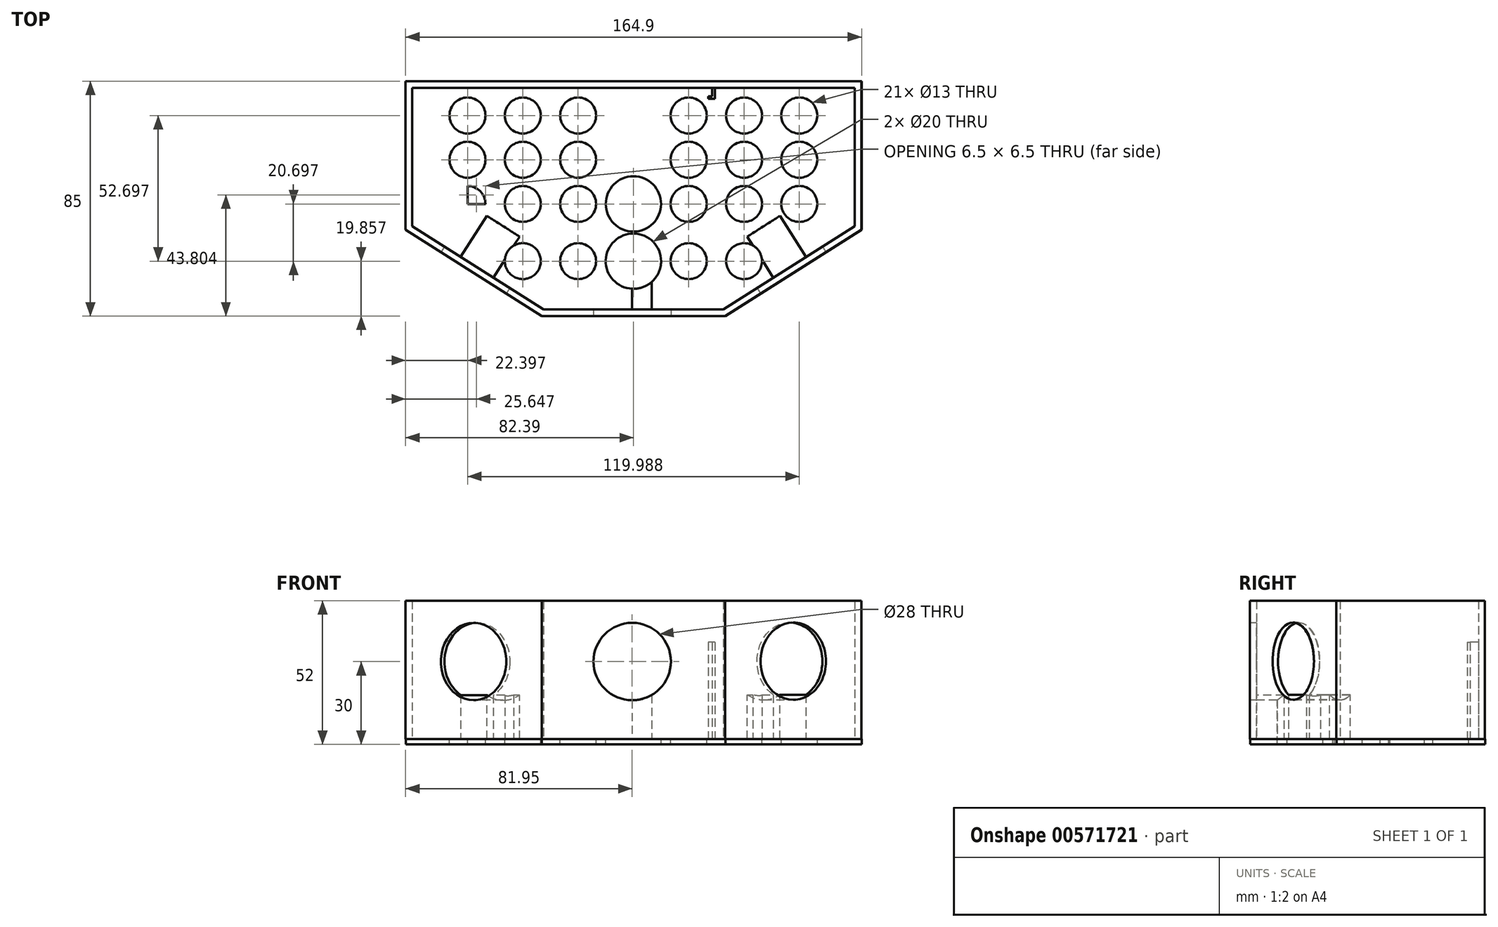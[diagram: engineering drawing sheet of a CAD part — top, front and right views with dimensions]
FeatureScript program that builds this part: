
annotation { "Feature Type Name" : "Feature", "Feature Type Description" : "" }
export const myFeature = defineFeature(function(context is Context, id is Id, definition is map)
    precondition{}
    {
        {
            var Q0;
            Q0=qCreatedBy(makeId("Top.planeOp"),FACE);
            var sketch = newSketch(context, id + "F0", { "sketchPlane" : qUnion([Q0])});
            skLineSegment(sketch, "E0.bottom", {"start": v(80.43, 34.87) * mm, "end": v(29.94, 34.87) * mm});
            skLineSegment(sketch, "E0.top", {"start": v(32.94, -45.28) * mm, "end": v(-32.06, -45.28) * mm});
            skLineSegment(sketch, "E0.left", {"start": v(80.43, 34.87) * mm, "end": v(80.43, -15.13) * mm});
            skLineSegment(sketch, "E0.right", {"start": v(-79.55, 34.87) * mm, "end": v(-79.55, -15.13) * mm});
            skPoint(sketch, "E0.middle", {"position": v(0, 0) * mm});
            skPoint(sketch, "E1", {"position": v(-79.55, -15.13) * mm});
            skPoint(sketch, "E2", {"position": v(80.43, -15.13) * mm});
            skPoint(sketch, "E3", {"position": v(32.94, -45.28) * mm});
            skPoint(sketch, "E4", {"position": v(-32.06, -45.28) * mm});
            skLineSegment(sketch, "E5", {"start": v(-79.55, -15.13) * mm, "end": v(-32.06, -45.28) * mm});
            skLineSegment(sketch, "E6", {"start": v(32.94, -45.28) * mm, "end": v(80.43, -15.13) * mm});
            skLineSegment(sketch, "E7", {"start": v(-55.8, -30.2) * mm, "end": v(-44.16, -37.6) * mm});
            skLineSegment(sketch, "E8", {"start": v(0.44, -45.28) * mm, "end": v(14.24, -45.28) * mm});
            skLineSegment(sketch, "E9", {"start": v(56.69, -30.2) * mm, "end": v(45.04, -37.6) * mm});
            skLineSegment(sketch, "E10", {"start": v(0.44, 34.87) * mm, "end": v(28.94, 34.87) * mm});
            skLineSegment(sketch, "E11", {"start": v(28.94, 34.87) * mm, "end": v(28.94, 31.87) * mm});
            skLineSegment(sketch, "E12", {"start": v(28.94, 31.87) * mm, "end": v(27.44, 31.87) * mm});
            skLineSegment(sketch, "E13", {"start": v(0.44, 34.87) * mm, "end": v(-28.06, 34.87) * mm});
            skLineSegment(sketch, "E14", {"start": v(-28.06, 31.87) * mm, "end": v(-26.56, 31.87) * mm});
            skLineSegment(sketch, "E15", {"start": v(-26.56, 31.87) * mm, "end": v(-28.06, 31.87) * mm});
            skLineSegment(sketch, "E16", {"start": v(-28.06, 34.87) * mm, "end": v(-28.06, 31.87) * mm});
            skLineSegment(sketch, "E17.0", {"start": v(82.83, 37.27) * mm, "end": v(-81.95, 37.27) * mm});
            skLineSegment(sketch, "E17.1", {"start": v(33.64, -47.68) * mm, "end": v(82.83, -16.45) * mm});
            skLineSegment(sketch, "E17.2", {"start": v(33.64, -47.68) * mm, "end": v(-32.76, -47.68) * mm});
            skLineSegment(sketch, "E17.3", {"start": v(82.83, 37.27) * mm, "end": v(82.83, -16.45) * mm});
            skLineSegment(sketch, "E17.4", {"start": v(-81.95, -16.45) * mm, "end": v(-32.76, -47.68) * mm});
            skLineSegment(sketch, "E17.5", {"start": v(-81.95, 37.27) * mm, "end": v(-81.95, -16.45) * mm});
            skLineSegment(sketch, "E18.0", {"start": v(-26.56, 30.87) * mm, "end": v(-29.06, 30.87) * mm});
            skLineSegment(sketch, "E18.1", {"start": v(-29.06, 34.87) * mm, "end": v(-29.06, 30.87) * mm});
            skLineSegment(sketch, "E19.0", {"start": v(29.94, 30.87) * mm, "end": v(27.44, 30.87) * mm});
            skLineSegment(sketch, "E19.1", {"start": v(29.94, 34.87) * mm, "end": v(29.94, 30.87) * mm});
            skLineSegment(sketch, "E20", {"start": v(-26.56, 30.87) * mm, "end": v(-26.56, 31.87) * mm});
            skLineSegment(sketch, "E21", {"start": v(27.44, 30.87) * mm, "end": v(27.44, 31.87) * mm});
            skLineSegment(sketch, "E22.trimOffspring", {"start": v(-29.06, 34.87) * mm, "end": v(-79.55, 34.87) * mm});
            skLineSegment(sketch, "E23.trimOffspring", {"start": v(28.94, 34.87) * mm, "end": v(-28.06, 34.87) * mm});
            skLineSegment(sketch, "E24", {"start": v(-79.55, 34.87) * mm, "end": v(-59.55, 34.87) * mm});
            skLineSegment(sketch, "E25", {"start": v(80.43, 34.87) * mm, "end": v(60.43, 34.87) * mm});
            skLineSegment(sketch, "E26", {"start": v(-59.55, 34.87) * mm, "end": v(-59.55, -27.82) * mm});
            skLineSegment(sketch, "E27", {"start": v(-59.55, -27.82) * mm, "end": v(60.43, -27.82) * mm});
            skLineSegment(sketch, "E28", {"start": v(60.43, -27.82) * mm, "end": v(60.43, 34.87) * mm});
            skLineSegment(sketch, "E29", {"start": v(60.43, 34.87) * mm, "end": v(60.43, 24.87) * mm});
            skLineSegment(sketch, "E30", {"start": v(60.43, 24.87) * mm, "end": v(-59.55, 24.87) * mm});
            skLineSegment(sketch, "E31", {"start": v(-59.55, 34.87) * mm, "end": v(-39.55, 34.87) * mm});
            skLineSegment(sketch, "E32", {"start": v(-39.55, 34.87) * mm, "end": v(-19.55, 34.87) * mm});
            skLineSegment(sketch, "E33", {"start": v(60.43, 34.87) * mm, "end": v(40.43, 34.87) * mm});
            skLineSegment(sketch, "E34", {"start": v(40.43, 34.87) * mm, "end": v(20.43, 34.87) * mm});
            skLineSegment(sketch, "E35", {"start": v(60.43, -27.82) * mm, "end": v(40.43, -27.82) * mm});
            skLineSegment(sketch, "E36", {"start": v(40.43, -27.82) * mm, "end": v(20.43, -27.82) * mm});
            skLineSegment(sketch, "E37", {"start": v(-59.55, -27.82) * mm, "end": v(-39.55, -27.82) * mm});
            skLineSegment(sketch, "E38", {"start": v(-39.55, -27.82) * mm, "end": v(-19.55, -27.82) * mm});
            skLineSegment(sketch, "E39", {"start": v(-39.55, 34.87) * mm, "end": v(-39.55, -27.82) * mm});
            skLineSegment(sketch, "E40", {"start": v(-19.55, -27.82) * mm, "end": v(-19.55, 34.87) * mm});
            skLineSegment(sketch, "E41", {"start": v(20.43, 34.87) * mm, "end": v(20.43, -27.82) * mm});
            skLineSegment(sketch, "E42", {"start": v(40.43, -27.82) * mm, "end": v(40.43, 34.87) * mm});
            skCircle(sketch, "E43", {"center": v(-59.55, 24.87) * mm, "radius": 6.5 * mm});
            skCircle(sketch, "E44", {"center": v(-19.55, -27.82) * mm, "radius": 6.5 * mm});
            skCircle(sketch, "E45", {"center": v(20.43, -27.82) * mm, "radius": 6.5 * mm});
            skLineSegment(sketch, "E46", {"start": v(-59.55, 24.87) * mm, "end": v(-39.55, 24.87) * mm});
            skLineSegment(sketch, "E47", {"start": v(-39.55, 24.87) * mm, "end": v(-19.55, 24.87) * mm});
            skLineSegment(sketch, "E48", {"start": v(-19.55, 24.87) * mm, "end": v(20.43, 24.87) * mm});
            skLineSegment(sketch, "E49", {"start": v(20.43, 24.87) * mm, "end": v(40.43, 24.87) * mm});
            skLineSegment(sketch, "E50", {"start": v(40.43, 24.87) * mm, "end": v(60.43, 24.87) * mm});
            skCircle(sketch, "E51", {"center": v(-39.55, 24.87) * mm, "radius": 6.5 * mm});
            skCircle(sketch, "E52", {"center": v(-19.55, 24.87) * mm, "radius": 6.5 * mm});
            skCircle(sketch, "E53", {"center": v(20.43, 24.87) * mm, "radius": 6.5 * mm});
            skCircle(sketch, "E54", {"center": v(40.43, 24.87) * mm, "radius": 6.5 * mm});
            skCircle(sketch, "E55", {"center": v(60.43, 24.87) * mm, "radius": 6.5 * mm});
            skLineSegment(sketch, "E56", {"start": v(-59.55, 24.87) * mm, "end": v(-59.55, 8.87) * mm});
            skLineSegment(sketch, "E57", {"start": v(-59.55, 8.87) * mm, "end": v(-59.55, -7.13) * mm});
            skLineSegment(sketch, "E58", {"start": v(-59.55, -7.13) * mm, "end": v(-59.55, -11.32) * mm});
            skLineSegment(sketch, "E59", {"start": v(60.43, 24.87) * mm, "end": v(60.43, 8.87) * mm});
            skLineSegment(sketch, "E60", {"start": v(60.43, 8.87) * mm, "end": v(60.43, -7.13) * mm});
            skLineSegment(sketch, "E61", {"start": v(-59.55, 8.87) * mm, "end": v(60.43, 8.87) * mm});
            skLineSegment(sketch, "E62", {"start": v(60.43, -7.13) * mm, "end": v(-59.55, -7.13) * mm});
            skLineSegment(sketch, "E63", {"start": v(-39.55, 8.87) * mm, "end": v(-19.55, 8.87) * mm});
            skLineSegment(sketch, "E64", {"start": v(-19.55, 8.87) * mm, "end": v(-19.55, -7.13) * mm});
            skLineSegment(sketch, "E65", {"start": v(-19.55, -7.13) * mm, "end": v(-39.55, -7.13) * mm});
            skLineSegment(sketch, "E66", {"start": v(-39.55, -7.13) * mm, "end": v(-19.55, -7.13) * mm});
            skLineSegment(sketch, "E67", {"start": v(20.43, 8.87) * mm, "end": v(40.43, 8.87) * mm});
            skLineSegment(sketch, "E68", {"start": v(40.43, 8.87) * mm, "end": v(60.43, 8.87) * mm});
            skLineSegment(sketch, "E69", {"start": v(60.43, -7.13) * mm, "end": v(40.43, -7.13) * mm});
            skLineSegment(sketch, "E70", {"start": v(40.43, -7.13) * mm, "end": v(20.43, -7.13) * mm});
            skCircle(sketch, "E71", {"center": v(-59.55, 8.87) * mm, "radius": 6.5 * mm});
            skCircle(sketch, "E72", {"center": v(-59.55, -7.13) * mm, "radius": 6.5 * mm});
            skCircle(sketch, "E73", {"center": v(-39.55, -7.13) * mm, "radius": 6.5 * mm});
            skCircle(sketch, "E74", {"center": v(-39.55, 8.87) * mm, "radius": 6.5 * mm});
            skCircle(sketch, "E75", {"center": v(-19.55, 8.87) * mm, "radius": 6.5 * mm});
            skCircle(sketch, "E76", {"center": v(-19.55, -7.13) * mm, "radius": 6.5 * mm});
            skCircle(sketch, "E77", {"center": v(20.43, 8.87) * mm, "radius": 6.5 * mm});
            skCircle(sketch, "E78", {"center": v(40.43, 8.87) * mm, "radius": 6.5 * mm});
            skCircle(sketch, "E79", {"center": v(60.43, 8.87) * mm, "radius": 6.5 * mm});
            skCircle(sketch, "E80", {"center": v(60.43, -7.13) * mm, "radius": 6.5 * mm});
            skCircle(sketch, "E81", {"center": v(40.43, -7.13) * mm, "radius": 6.5 * mm});
            skCircle(sketch, "E82", {"center": v(20.43, -7.13) * mm, "radius": 6.5 * mm});
            skLineSegment(sketch, "E83", {"start": v(-19.55, -27.82) * mm, "end": v(0.44, -27.82) * mm});
            skLineSegment(sketch, "E84", {"start": v(0.44, -27.82) * mm, "end": v(0.44, 34.87) * mm});
            skLineSegment(sketch, "E85", {"start": v(0.44, 24.87) * mm, "end": v(0.44, 8.87) * mm});
            skLineSegment(sketch, "E86", {"start": v(0.44, 8.87) * mm, "end": v(0.44, -7.13) * mm});
            skLineSegment(sketch, "E87", {"start": v(0.44, -7.13) * mm, "end": v(0.44, -27.82) * mm});
            skCircle(sketch, "E88", {"center": v(0.44, -27.82) * mm, "radius": 10 * mm});
            skCircle(sketch, "E89", {"center": v(0.44, -7.13) * mm, "radius": 10 * mm});
            skCircle(sketch, "E90", {"center": v(0.44, 24.87) * mm, "radius": 9.5 * mm});
            skCircle(sketch, "E91", {"center": v(-39.55, -27.82) * mm, "radius": 6.5 * mm});
            skCircle(sketch, "E92", {"center": v(40.43, -27.82) * mm, "radius": 6.5 * mm});
            skSolve(sketch);
        }
        {
            var Q0;
            Q0 = qSketchRegion(id + "F0", true);
            extrude(context, id + "F1", {"entities" : qUnion([Q0]), "depth" : 50 * mm, "offsetDistance" : 25 * mm});
        }
        {
            var Q0;
            Q0=qCreatedBy(makeId("Top.planeOp"),FACE);
            var sketch = newSketch(context, id + "F2", { "sketchPlane" : qUnion([Q0])});
            skLineSegment(sketch, "E93.0", {"start": v(82.95, 37.32) * mm, "end": v(-81.84, 37.32) * mm});
            skLineSegment(sketch, "E93.1", {"start": v(33.75, -47.63) * mm, "end": v(82.95, -16.4) * mm});
            skLineSegment(sketch, "E93.2", {"start": v(33.75, -47.63) * mm, "end": v(-32.64, -47.63) * mm});
            skLineSegment(sketch, "E93.3", {"start": v(82.95, 37.32) * mm, "end": v(82.95, -16.4) * mm});
            skLineSegment(sketch, "E93.4", {"start": v(-81.84, -16.4) * mm, "end": v(-32.64, -47.63) * mm});
            skLineSegment(sketch, "E93.5", {"start": v(-81.84, 37.32) * mm, "end": v(-81.84, -16.4) * mm});
            skSolve(sketch);
        }
        {
            var Q0;
            Q0=makeQuery(id+"F1.opExtrude","SWEPT_FACE",FACE,{"disambiguationData":[OSD([sQuery(id+"F0.wireOp",EDGE,"E17.1")])]});
            var sketch = newSketch(context, id + "F3", { "sketchPlane" : qUnion([Q0])});
            skCircle(sketch, "E94", {"center": v(31.98, 28.12) * mm, "radius": 14 * mm});
            skLineSegment(sketch, "E95", {"start": v(31.98, 14.12) * mm, "end": v(31.98, 0) * mm});
            skPoint(sketch, "E95.startSnap0", {"position": v(31.98, 0) * mm});
            skLineSegment(sketch, "E96", {"start": v(31.98, 0) * mm, "end": v(38.98, 0) * mm});
            skLineSegment(sketch, "E97", {"start": v(31.98, 0) * mm, "end": v(24.98, 0) * mm});
            skLineSegment(sketch, "E98", {"start": v(24.98, 0) * mm, "end": v(24.98, 16) * mm});
            skLineSegment(sketch, "E99", {"start": v(38.98, 0) * mm, "end": v(38.98, 16) * mm});
            skSolve(sketch);
        }
        {
            var Q0;
            Q0=makeQuery(id+"F3.imprint","IMPRINT",FACE,{"disambiguationData":[TD([[makeQuery(id+"F3.imprint","IMPRINT",EDGE,{"derivedFrom":sQuery(id+"F3.wireOp",EDGE,"E94")}),1.0]])]});
            extrude(context, id + "F4", {"entities" : qUnion([Q0]), "operationType" : NewBodyOperationType.REMOVE, "oppositeDirection" : true, "depth" : 28 * mm, "offsetDistance" : 25 * mm});
        }
        {
            var Q0;
            Q0=makeQuery(id+"F1.opExtrude","SWEPT_FACE",FACE,{"disambiguationData":[OSD([sQuery(id+"F0.wireOp",EDGE,"E17.2")])]});
            var sketch = newSketch(context, id + "F5", { "sketchPlane" : qUnion([Q0])});
            skLineSegment(sketch, "E100", {"start": v(0, 0) * mm, "end": v(0, 28) * mm});
            skLineSegment(sketch, "E101", {"start": v(0, 28) * mm, "end": v(14, 28) * mm});
            skCircle(sketch, "E102", {"center": v(0, 28) * mm, "radius": 14 * mm});
            skLineSegment(sketch, "E103", {"start": v(0, 0) * mm, "end": v(-7, 0) * mm});
            skLineSegment(sketch, "E104", {"start": v(-7, 0) * mm, "end": v(0, 0) * mm});
            skLineSegment(sketch, "E105", {"start": v(-7, 0) * mm, "end": v(-7, 15.88) * mm});
            skLineSegment(sketch, "E106", {"start": v(-7, 15.88) * mm, "end": v(-7, 0) * mm});
            skLineSegment(sketch, "E107", {"start": v(0, 0) * mm, "end": v(7, 0) * mm});
            skLineSegment(sketch, "E108", {"start": v(7, 0) * mm, "end": v(7, 15.88) * mm});
            skLineSegment(sketch, "E109", {"start": v(7, 15.88) * mm, "end": v(7, 0) * mm});
            skSolve(sketch);
        }
        {
            var Q0;
            Q0 = qSketchRegion(id + "F2", true);
            extrude(context, id + "F6", {"entities" : qUnion([Q0]), "operationType" : NewBodyOperationType.ADD, "oppositeDirection" : true, "depth" : 2 * mm, "offsetDistance" : 25 * mm});
        }
        {
            var Q0;
            {var subQ0=sQuery(id+"F5.wireOp",EDGE,"E101");Q0=makeQuery(id+"F5.imprint","IMPRINT",FACE,{"disambiguationData":[TD([[makeQuery(id+"F5.imprint","IMPRINT",EDGE,{"derivedFrom":subQ0}),-1.0]])]});}
            var Q1;
            {var subQ0=sQuery(id+"F5.wireOp",EDGE,"E101");Q1=makeQuery(id+"F5.imprint","IMPRINT",FACE,{"disambiguationData":[TD([[makeQuery(id+"F5.imprint","IMPRINT",EDGE,{"derivedFrom":subQ0}),1.0]])]});}
            extrude(context, id + "F7", {"entities" : qUnion([Q0, Q1]), "operationType" : NewBodyOperationType.REMOVE, "oppositeDirection" : true, "depth" : 20.7 * mm, "offsetDistance" : 25 * mm});
        }
        {
            var Q0;
            Q0=makeQuery(id+"F1.opExtrude","SWEPT_FACE",FACE,{"disambiguationData":[OSD([sQuery(id+"F0.wireOp",EDGE,"E17.4")])]});
            var sketch = newSketch(context, id + "F8", { "sketchPlane" : qUnion([Q0])});
            skLineSegment(sketch, "E110", {"start": v(-31.24, 0) * mm, "end": v(-31.24, 28) * mm});
            skLineSegment(sketch, "E111", {"start": v(-31.24, 28) * mm, "end": v(-45.24, 28) * mm});
            skCircle(sketch, "E112", {"center": v(-31.24, 28) * mm, "radius": 14 * mm});
            skLineSegment(sketch, "E113", {"start": v(-31.24, 0) * mm, "end": v(-38.24, 0) * mm});
            skLineSegment(sketch, "E114", {"start": v(-38.24, 0) * mm, "end": v(-38.24, 15.88) * mm});
            skLineSegment(sketch, "E115", {"start": v(-24.24, 0) * mm, "end": v(-24.24, 15.88) * mm});
            skSolve(sketch);
        }
        {
            var Q0;
            {var subQ0=sQuery(id+"F8.wireOp",EDGE,"E111");Q0=makeQuery(id+"F8.imprint","IMPRINT",FACE,{"disambiguationData":[TD([[makeQuery(id+"F8.imprint","IMPRINT",EDGE,{"derivedFrom":subQ0}),-1.0]])]});}
            var Q1;
            {var subQ0=sQuery(id+"F8.wireOp",EDGE,"E111");Q1=makeQuery(id+"F8.imprint","IMPRINT",FACE,{"disambiguationData":[TD([[makeQuery(id+"F8.imprint","IMPRINT",EDGE,{"derivedFrom":subQ0}),1.0]])]});}
            extrude(context, id + "F9", {"entities" : qUnion([Q0, Q1]), "operationType" : NewBodyOperationType.REMOVE, "oppositeDirection" : true, "depth" : 25 * mm, "offsetDistance" : 25 * mm});
        }
        {
            var Q0;
            {var subQ0=sQuery(id+"F5.wireOp",EDGE,"E104");Q0=makeQuery(id+"F5.imprint","IMPRINT",FACE,{"disambiguationData":[TD([[makeQuery(id+"F5.imprint","IMPRINT",EDGE,{"derivedFrom":subQ0}),-1.0]])]});}
            var Q1;
            {var subQ0=sQuery(id+"F5.wireOp",EDGE,"E107");Q1=makeQuery(id+"F5.imprint","IMPRINT",FACE,{"disambiguationData":[TD([[makeQuery(id+"F5.imprint","IMPRINT",EDGE,{"derivedFrom":subQ0}),-1.0]])]});}
            extrude(context, id + "F10", {"entities" : qUnion([Q0, Q1]), "operationType" : NewBodyOperationType.ADD, "oppositeDirection" : true, "depth" : 20 * mm, "offsetDistance" : 25 * mm});
        }
        {
            var Q0;
            {var subQ0=sQuery(id+"F8.wireOp",EDGE,"E113");Q0=makeQuery(id+"F8.imprint","IMPRINT",FACE,{"disambiguationData":[TD([[makeQuery(id+"F8.imprint","IMPRINT",EDGE,{"derivedFrom":subQ0}),1.0]])]});}
            var Q1;
            {var subQ6=sQuery(id+"F8.wireOp",EDGE,"E115");Q1=makeQuery(id+"F8.imprint","IMPRINT",FACE,{"disambiguationData":[TD([[makeQuery(id+"F8.imprint","IMPRINT",EDGE,{"derivedFrom":subQ6}),1.0]])]});}
            extrude(context, id + "F11", {"entities" : qUnion([Q0, Q1]), "operationType" : NewBodyOperationType.ADD, "oppositeDirection" : true, "depth" : 20 * mm, "offsetDistance" : 25 * mm});
        }
        {
            var Q0;
            {var subQ0=sQuery(id+"F3.wireOp",EDGE,"E95");Q0=makeQuery(id+"F3.imprint","IMPRINT",FACE,{"disambiguationData":[TD([[makeQuery(id+"F3.imprint","IMPRINT",EDGE,{"derivedFrom":subQ0}),-1.0]])]});}
            var Q1;
            {var subQ0=sQuery(id+"F3.wireOp",EDGE,"E95");Q1=makeQuery(id+"F3.imprint","IMPRINT",FACE,{"disambiguationData":[TD([[makeQuery(id+"F3.imprint","IMPRINT",EDGE,{"derivedFrom":subQ0}),1.0]])]});}
            extrude(context, id + "F12", {"entities" : qUnion([Q0, Q1]), "operationType" : NewBodyOperationType.ADD, "oppositeDirection" : true, "depth" : 20 * mm, "offsetDistance" : 25 * mm});
        }
        {
            var Q0;
            {var subQ1=sQuery(id+"F0.wireOp",EDGE,"E26");var subQ3=sQuery(id+"F0.wireOp",EDGE,"E43");var subQ4=makeQuery(id+"F0.imprint","INTERSECT",VERTEX,{"derivedFrom":[subQ1,subQ3]});Q0=makeQuery(id+"F0.imprint","IMPRINT",FACE,{"disambiguationData":[TD([[makeQuery(id+"F0.imprint","IMPRINT",EDGE,{"disambiguationData":[TD([[subQ4,-1.0]])],"derivedFrom":subQ3}),1.0]])]});}
            var Q1;
            {var subQ1=sQuery(id+"F0.wireOp",EDGE,"E26");var subQ3=sQuery(id+"F0.wireOp",EDGE,"E43");var subQ4=makeQuery(id+"F0.imprint","INTERSECT",VERTEX,{"derivedFrom":[subQ1,subQ3]});Q1=makeQuery(id+"F0.imprint","IMPRINT",FACE,{"disambiguationData":[TD([[makeQuery(id+"F0.imprint","IMPRINT",EDGE,{"disambiguationData":[TD([[subQ4,1.0]])],"derivedFrom":subQ3}),1.0]])]});}
            var Q2;
            {var subQ0=sQuery(id+"F0.wireOp",EDGE,"E46");var subQ1=sQuery(id+"F0.wireOp",EDGE,"E43");var subQ2=makeQuery(id+"F0.imprint","INTERSECT",VERTEX,{"derivedFrom":[subQ1,subQ0]});Q2=makeQuery(id+"F0.imprint","IMPRINT",FACE,{"disambiguationData":[TD([[makeQuery(id+"F0.imprint","IMPRINT",EDGE,{"disambiguationData":[TD([[subQ2,1.0]])],"derivedFrom":subQ1}),1.0]])]});}
            var Q3;
            {var subQ1=sQuery(id+"F0.wireOp",EDGE,"E39");var subQ3=sQuery(id+"F0.wireOp",EDGE,"E51");var subQ4=makeQuery(id+"F0.imprint","INTERSECT",VERTEX,{"disambiguationData":[OD(0.0)],"derivedFrom":[subQ1,subQ3]});Q3=makeQuery(id+"F0.imprint","IMPRINT",FACE,{"disambiguationData":[TD([[makeQuery(id+"F0.imprint","IMPRINT",EDGE,{"disambiguationData":[TD([[subQ4,-1.0]])],"derivedFrom":subQ3}),1.0]])]});}
            var Q4;
            {var subQ1=sQuery(id+"F0.wireOp",EDGE,"E39");var subQ3=sQuery(id+"F0.wireOp",EDGE,"E51");var subQ4=makeQuery(id+"F0.imprint","INTERSECT",VERTEX,{"disambiguationData":[OD(0.0)],"derivedFrom":[subQ1,subQ3]});Q4=makeQuery(id+"F0.imprint","IMPRINT",FACE,{"disambiguationData":[TD([[makeQuery(id+"F0.imprint","IMPRINT",EDGE,{"disambiguationData":[TD([[subQ4,1.0]])],"derivedFrom":subQ3}),1.0]])]});}
            var Q5;
            {var subQ1=sQuery(id+"F0.wireOp",EDGE,"E39");var subQ3=sQuery(id+"F0.wireOp",EDGE,"E51");var subQ4=makeQuery(id+"F0.imprint","INTERSECT",VERTEX,{"disambiguationData":[OD(1.0)],"derivedFrom":[subQ1,subQ3]});Q5=makeQuery(id+"F0.imprint","IMPRINT",FACE,{"disambiguationData":[TD([[makeQuery(id+"F0.imprint","IMPRINT",EDGE,{"disambiguationData":[TD([[subQ4,-1.0]])],"derivedFrom":subQ3}),1.0]])]});}
            var Q6;
            {var subQ1=sQuery(id+"F0.wireOp",EDGE,"E39");var subQ3=sQuery(id+"F0.wireOp",EDGE,"E51");var subQ4=makeQuery(id+"F0.imprint","INTERSECT",VERTEX,{"disambiguationData":[OD(1.0)],"derivedFrom":[subQ1,subQ3]});Q6=makeQuery(id+"F0.imprint","IMPRINT",FACE,{"disambiguationData":[TD([[makeQuery(id+"F0.imprint","IMPRINT",EDGE,{"disambiguationData":[TD([[subQ4,1.0]])],"derivedFrom":subQ3}),1.0]])]});}
            var Q7;
            {var subQ1=sQuery(id+"F0.wireOp",EDGE,"E40");var subQ3=sQuery(id+"F0.wireOp",EDGE,"E52");var subQ4=makeQuery(id+"F0.imprint","INTERSECT",VERTEX,{"disambiguationData":[OD(1.0)],"derivedFrom":[subQ1,subQ3]});Q7=makeQuery(id+"F0.imprint","IMPRINT",FACE,{"disambiguationData":[TD([[makeQuery(id+"F0.imprint","IMPRINT",EDGE,{"disambiguationData":[TD([[subQ4,-1.0]])],"derivedFrom":subQ3}),1.0]])]});}
            var Q8;
            {var subQ1=sQuery(id+"F0.wireOp",EDGE,"E40");var subQ3=sQuery(id+"F0.wireOp",EDGE,"E52");var subQ4=makeQuery(id+"F0.imprint","INTERSECT",VERTEX,{"disambiguationData":[OD(1.0)],"derivedFrom":[subQ1,subQ3]});Q8=makeQuery(id+"F0.imprint","IMPRINT",FACE,{"disambiguationData":[TD([[makeQuery(id+"F0.imprint","IMPRINT",EDGE,{"disambiguationData":[TD([[subQ4,1.0]])],"derivedFrom":subQ3}),1.0]])]});}
            var Q9;
            {var subQ1=sQuery(id+"F0.wireOp",EDGE,"E40");var subQ3=sQuery(id+"F0.wireOp",EDGE,"E52");var subQ4=makeQuery(id+"F0.imprint","INTERSECT",VERTEX,{"disambiguationData":[OD(0.0)],"derivedFrom":[subQ1,subQ3]});Q9=makeQuery(id+"F0.imprint","IMPRINT",FACE,{"disambiguationData":[TD([[makeQuery(id+"F0.imprint","IMPRINT",EDGE,{"disambiguationData":[TD([[subQ4,-1.0]])],"derivedFrom":subQ3}),1.0]])]});}
            var Q10;
            {var subQ1=sQuery(id+"F0.wireOp",EDGE,"E40");var subQ3=sQuery(id+"F0.wireOp",EDGE,"E52");var subQ4=makeQuery(id+"F0.imprint","INTERSECT",VERTEX,{"disambiguationData":[OD(0.0)],"derivedFrom":[subQ1,subQ3]});Q10=makeQuery(id+"F0.imprint","IMPRINT",FACE,{"disambiguationData":[TD([[makeQuery(id+"F0.imprint","IMPRINT",EDGE,{"disambiguationData":[TD([[subQ4,1.0]])],"derivedFrom":subQ3}),1.0]])]});}
            var Q11;
            {var subQ1=sQuery(id+"F0.wireOp",EDGE,"E39");var subQ3=sQuery(id+"F0.wireOp",EDGE,"E74");var subQ4=makeQuery(id+"F0.imprint","INTERSECT",VERTEX,{"disambiguationData":[OD(0.0)],"derivedFrom":[subQ1,subQ3]});Q11=makeQuery(id+"F0.imprint","IMPRINT",FACE,{"disambiguationData":[TD([[makeQuery(id+"F0.imprint","IMPRINT",EDGE,{"disambiguationData":[TD([[subQ4,1.0]])],"derivedFrom":subQ3}),1.0]])]});}
            var Q12;
            {var subQ1=sQuery(id+"F0.wireOp",EDGE,"E39");var subQ3=sQuery(id+"F0.wireOp",EDGE,"E74");var subQ4=makeQuery(id+"F0.imprint","INTERSECT",VERTEX,{"disambiguationData":[OD(0.0)],"derivedFrom":[subQ1,subQ3]});Q12=makeQuery(id+"F0.imprint","IMPRINT",FACE,{"disambiguationData":[TD([[makeQuery(id+"F0.imprint","IMPRINT",EDGE,{"disambiguationData":[TD([[subQ4,-1.0]])],"derivedFrom":subQ3}),1.0]])]});}
            var Q13;
            {var subQ1=sQuery(id+"F0.wireOp",EDGE,"E39");var subQ3=sQuery(id+"F0.wireOp",EDGE,"E74");var subQ4=makeQuery(id+"F0.imprint","INTERSECT",VERTEX,{"disambiguationData":[OD(1.0)],"derivedFrom":[subQ1,subQ3]});Q13=makeQuery(id+"F0.imprint","IMPRINT",FACE,{"disambiguationData":[TD([[makeQuery(id+"F0.imprint","IMPRINT",EDGE,{"disambiguationData":[TD([[subQ4,1.0]])],"derivedFrom":subQ3}),1.0]])]});}
            var Q14;
            {var subQ1=sQuery(id+"F0.wireOp",EDGE,"E39");var subQ3=sQuery(id+"F0.wireOp",EDGE,"E74");var subQ4=makeQuery(id+"F0.imprint","INTERSECT",VERTEX,{"disambiguationData":[OD(1.0)],"derivedFrom":[subQ1,subQ3]});Q14=makeQuery(id+"F0.imprint","IMPRINT",FACE,{"disambiguationData":[TD([[makeQuery(id+"F0.imprint","IMPRINT",EDGE,{"disambiguationData":[TD([[subQ4,-1.0]])],"derivedFrom":subQ3}),1.0]])]});}
            var Q15;
            {var subQ1=sQuery(id+"F0.wireOp",EDGE,"E56");var subQ3=sQuery(id+"F0.wireOp",EDGE,"E71");var subQ4=makeQuery(id+"F0.imprint","INTERSECT",VERTEX,{"derivedFrom":[subQ1,subQ3]});Q15=makeQuery(id+"F0.imprint","IMPRINT",FACE,{"disambiguationData":[TD([[makeQuery(id+"F0.imprint","IMPRINT",EDGE,{"disambiguationData":[TD([[subQ4,-1.0]])],"derivedFrom":subQ3}),1.0]])]});}
            var Q16;
            {var subQ1=sQuery(id+"F0.wireOp",EDGE,"E56");var subQ3=sQuery(id+"F0.wireOp",EDGE,"E71");var subQ4=makeQuery(id+"F0.imprint","INTERSECT",VERTEX,{"derivedFrom":[subQ1,subQ3]});Q16=makeQuery(id+"F0.imprint","IMPRINT",FACE,{"disambiguationData":[TD([[makeQuery(id+"F0.imprint","IMPRINT",EDGE,{"disambiguationData":[TD([[subQ4,1.0]])],"derivedFrom":subQ3}),1.0]])]});}
            var Q17;
            {var subQ1=sQuery(id+"F0.wireOp",EDGE,"E57");var subQ3=sQuery(id+"F0.wireOp",EDGE,"E71");var subQ4=makeQuery(id+"F0.imprint","INTERSECT",VERTEX,{"derivedFrom":[subQ1,subQ3]});Q17=makeQuery(id+"F0.imprint","IMPRINT",FACE,{"disambiguationData":[TD([[makeQuery(id+"F0.imprint","IMPRINT",EDGE,{"disambiguationData":[TD([[subQ4,-1.0]])],"derivedFrom":subQ3}),1.0]])]});}
            var Q18;
            {var subQ1=sQuery(id+"F0.wireOp",EDGE,"E57");var subQ3=sQuery(id+"F0.wireOp",EDGE,"E72");var subQ4=makeQuery(id+"F0.imprint","INTERSECT",VERTEX,{"derivedFrom":[subQ1,subQ3]});Q18=makeQuery(id+"F0.imprint","IMPRINT",FACE,{"disambiguationData":[TD([[makeQuery(id+"F0.imprint","IMPRINT",EDGE,{"disambiguationData":[TD([[subQ4,-1.0]])],"derivedFrom":subQ3}),1.0]])]});}
            var Q19;
            {var subQ1=sQuery(id+"F0.wireOp",EDGE,"E58");var subQ3=sQuery(id+"F0.wireOp",EDGE,"E72");var subQ4=makeQuery(id+"F0.imprint","INTERSECT",VERTEX,{"derivedFrom":[subQ1,subQ3]});Q19=makeQuery(id+"F0.imprint","IMPRINT",FACE,{"disambiguationData":[TD([[makeQuery(id+"F0.imprint","IMPRINT",EDGE,{"disambiguationData":[TD([[subQ4,-1.0]])],"derivedFrom":subQ3}),1.0]])]});}
            var Q20;
            {var subQ1=sQuery(id+"F0.wireOp",EDGE,"E57");var subQ3=sQuery(id+"F0.wireOp",EDGE,"E72");var subQ4=makeQuery(id+"F0.imprint","INTERSECT",VERTEX,{"derivedFrom":[subQ1,subQ3]});Q20=makeQuery(id+"F0.imprint","IMPRINT",FACE,{"disambiguationData":[TD([[makeQuery(id+"F0.imprint","IMPRINT",EDGE,{"disambiguationData":[TD([[subQ4,1.0]])],"derivedFrom":subQ3}),1.0]])]});}
            var Q21;
            {var subQ1=sQuery(id+"F0.wireOp",EDGE,"E39");var subQ3=sQuery(id+"F0.wireOp",EDGE,"E73");var subQ4=makeQuery(id+"F0.imprint","INTERSECT",VERTEX,{"disambiguationData":[OD(0.0)],"derivedFrom":[subQ1,subQ3]});Q21=makeQuery(id+"F0.imprint","IMPRINT",FACE,{"disambiguationData":[TD([[makeQuery(id+"F0.imprint","IMPRINT",EDGE,{"disambiguationData":[TD([[subQ4,-1.0]])],"derivedFrom":subQ3}),1.0]])]});}
            var Q22;
            {var subQ1=sQuery(id+"F0.wireOp",EDGE,"E39");var subQ3=sQuery(id+"F0.wireOp",EDGE,"E73");var subQ4=makeQuery(id+"F0.imprint","INTERSECT",VERTEX,{"disambiguationData":[OD(1.0)],"derivedFrom":[subQ1,subQ3]});Q22=makeQuery(id+"F0.imprint","IMPRINT",FACE,{"disambiguationData":[TD([[makeQuery(id+"F0.imprint","IMPRINT",EDGE,{"disambiguationData":[TD([[subQ4,1.0]])],"derivedFrom":subQ3}),1.0]])]});}
            var Q23;
            {var subQ1=sQuery(id+"F0.wireOp",EDGE,"E39");var subQ3=sQuery(id+"F0.wireOp",EDGE,"E73");var subQ4=makeQuery(id+"F0.imprint","INTERSECT",VERTEX,{"disambiguationData":[OD(0.0)],"derivedFrom":[subQ1,subQ3]});Q23=makeQuery(id+"F0.imprint","IMPRINT",FACE,{"disambiguationData":[TD([[makeQuery(id+"F0.imprint","IMPRINT",EDGE,{"disambiguationData":[TD([[subQ4,1.0]])],"derivedFrom":subQ3}),1.0]])]});}
            var Q24;
            {var subQ1=sQuery(id+"F0.wireOp",EDGE,"E39");var subQ3=sQuery(id+"F0.wireOp",EDGE,"E73");var subQ4=makeQuery(id+"F0.imprint","INTERSECT",VERTEX,{"disambiguationData":[OD(1.0)],"derivedFrom":[subQ1,subQ3]});Q24=makeQuery(id+"F0.imprint","IMPRINT",FACE,{"disambiguationData":[TD([[makeQuery(id+"F0.imprint","IMPRINT",EDGE,{"disambiguationData":[TD([[subQ4,-1.0]])],"derivedFrom":subQ3}),1.0]])]});}
            var Q25;
            {var subQ1=sQuery(id+"F0.wireOp",EDGE,"E64");var subQ3=sQuery(id+"F0.wireOp",EDGE,"E76");var subQ4=makeQuery(id+"F0.imprint","INTERSECT",VERTEX,{"derivedFrom":[subQ1,subQ3]});Q25=makeQuery(id+"F0.imprint","IMPRINT",FACE,{"disambiguationData":[TD([[makeQuery(id+"F0.imprint","IMPRINT",EDGE,{"disambiguationData":[TD([[subQ4,-1.0]])],"derivedFrom":subQ3}),1.0]])]});}
            var Q26;
            {var subQ1=sQuery(id+"F0.wireOp",EDGE,"E40");var subQ3=sQuery(id+"F0.wireOp",EDGE,"E76");var subQ4=makeQuery(id+"F0.imprint","INTERSECT",VERTEX,{"derivedFrom":[subQ1,subQ3]});Q26=makeQuery(id+"F0.imprint","IMPRINT",FACE,{"disambiguationData":[TD([[makeQuery(id+"F0.imprint","IMPRINT",EDGE,{"disambiguationData":[TD([[subQ4,1.0]])],"derivedFrom":subQ3}),1.0]])]});}
            var Q27;
            {var subQ1=sQuery(id+"F0.wireOp",EDGE,"E40");var subQ3=sQuery(id+"F0.wireOp",EDGE,"E76");var subQ4=makeQuery(id+"F0.imprint","INTERSECT",VERTEX,{"derivedFrom":[subQ1,subQ3]});Q27=makeQuery(id+"F0.imprint","IMPRINT",FACE,{"disambiguationData":[TD([[makeQuery(id+"F0.imprint","IMPRINT",EDGE,{"disambiguationData":[TD([[subQ4,-1.0]])],"derivedFrom":subQ3}),1.0]])]});}
            var Q28;
            {var subQ1=sQuery(id+"F0.wireOp",EDGE,"E62");var subQ3=sQuery(id+"F0.wireOp",EDGE,"E76");var subQ4=makeQuery(id+"F0.imprint","INTERSECT",VERTEX,{"derivedFrom":[subQ1,subQ3]});Q28=makeQuery(id+"F0.imprint","IMPRINT",FACE,{"disambiguationData":[TD([[makeQuery(id+"F0.imprint","IMPRINT",EDGE,{"disambiguationData":[TD([[subQ4,-1.0]])],"derivedFrom":subQ3}),1.0]])]});}
            var Q29;
            {var subQ1=sQuery(id+"F0.wireOp",EDGE,"E61");var subQ3=sQuery(id+"F0.wireOp",EDGE,"E75");var subQ4=makeQuery(id+"F0.imprint","INTERSECT",VERTEX,{"derivedFrom":[subQ1,subQ3]});Q29=makeQuery(id+"F0.imprint","IMPRINT",FACE,{"disambiguationData":[TD([[makeQuery(id+"F0.imprint","IMPRINT",EDGE,{"disambiguationData":[TD([[subQ4,1.0]])],"derivedFrom":subQ3}),1.0]])]});}
            var Q30;
            {var subQ1=sQuery(id+"F0.wireOp",EDGE,"E63");var subQ3=sQuery(id+"F0.wireOp",EDGE,"E75");var subQ4=makeQuery(id+"F0.imprint","INTERSECT",VERTEX,{"derivedFrom":[subQ1,subQ3]});Q30=makeQuery(id+"F0.imprint","IMPRINT",FACE,{"disambiguationData":[TD([[makeQuery(id+"F0.imprint","IMPRINT",EDGE,{"disambiguationData":[TD([[subQ4,-1.0]])],"derivedFrom":subQ3}),1.0]])]});}
            var Q31;
            {var subQ1=sQuery(id+"F0.wireOp",EDGE,"E40");var subQ3=sQuery(id+"F0.wireOp",EDGE,"E75");var subQ4=makeQuery(id+"F0.imprint","INTERSECT",VERTEX,{"derivedFrom":[subQ1,subQ3]});Q31=makeQuery(id+"F0.imprint","IMPRINT",FACE,{"disambiguationData":[TD([[makeQuery(id+"F0.imprint","IMPRINT",EDGE,{"disambiguationData":[TD([[subQ4,-1.0]])],"derivedFrom":subQ3}),1.0]])]});}
            var Q32;
            {var subQ1=sQuery(id+"F0.wireOp",EDGE,"E40");var subQ3=sQuery(id+"F0.wireOp",EDGE,"E75");var subQ4=makeQuery(id+"F0.imprint","INTERSECT",VERTEX,{"derivedFrom":[subQ1,subQ3]});Q32=makeQuery(id+"F0.imprint","IMPRINT",FACE,{"disambiguationData":[TD([[makeQuery(id+"F0.imprint","IMPRINT",EDGE,{"disambiguationData":[TD([[subQ4,1.0]])],"derivedFrom":subQ3}),1.0]])]});}
            var Q33;
            {var subQ1=sQuery(id+"F0.wireOp",EDGE,"E41");var subQ3=sQuery(id+"F0.wireOp",EDGE,"E53");var subQ4=makeQuery(id+"F0.imprint","INTERSECT",VERTEX,{"disambiguationData":[OD(1.0)],"derivedFrom":[subQ1,subQ3]});Q33=makeQuery(id+"F0.imprint","IMPRINT",FACE,{"disambiguationData":[TD([[makeQuery(id+"F0.imprint","IMPRINT",EDGE,{"disambiguationData":[TD([[subQ4,-1.0]])],"derivedFrom":subQ3}),1.0]])]});}
            var Q34;
            {var subQ1=sQuery(id+"F0.wireOp",EDGE,"E41");var subQ3=sQuery(id+"F0.wireOp",EDGE,"E53");var subQ4=makeQuery(id+"F0.imprint","INTERSECT",VERTEX,{"disambiguationData":[OD(0.0)],"derivedFrom":[subQ1,subQ3]});Q34=makeQuery(id+"F0.imprint","IMPRINT",FACE,{"disambiguationData":[TD([[makeQuery(id+"F0.imprint","IMPRINT",EDGE,{"disambiguationData":[TD([[subQ4,1.0]])],"derivedFrom":subQ3}),1.0]])]});}
            var Q35;
            {var subQ1=sQuery(id+"F0.wireOp",EDGE,"E41");var subQ3=sQuery(id+"F0.wireOp",EDGE,"E53");var subQ4=makeQuery(id+"F0.imprint","INTERSECT",VERTEX,{"disambiguationData":[OD(0.0)],"derivedFrom":[subQ1,subQ3]});Q35=makeQuery(id+"F0.imprint","IMPRINT",FACE,{"disambiguationData":[TD([[makeQuery(id+"F0.imprint","IMPRINT",EDGE,{"disambiguationData":[TD([[subQ4,-1.0]])],"derivedFrom":subQ3}),1.0]])]});}
            var Q36;
            {var subQ1=sQuery(id+"F0.wireOp",EDGE,"E41");var subQ3=sQuery(id+"F0.wireOp",EDGE,"E53");var subQ4=makeQuery(id+"F0.imprint","INTERSECT",VERTEX,{"disambiguationData":[OD(1.0)],"derivedFrom":[subQ1,subQ3]});Q36=makeQuery(id+"F0.imprint","IMPRINT",FACE,{"disambiguationData":[TD([[makeQuery(id+"F0.imprint","IMPRINT",EDGE,{"disambiguationData":[TD([[subQ4,1.0]])],"derivedFrom":subQ3}),1.0]])]});}
            var Q37;
            {var subQ1=sQuery(id+"F0.wireOp",EDGE,"E41");var subQ3=sQuery(id+"F0.wireOp",EDGE,"E77");var subQ4=makeQuery(id+"F0.imprint","INTERSECT",VERTEX,{"disambiguationData":[OD(0.0)],"derivedFrom":[subQ1,subQ3]});Q37=makeQuery(id+"F0.imprint","IMPRINT",FACE,{"disambiguationData":[TD([[makeQuery(id+"F0.imprint","IMPRINT",EDGE,{"disambiguationData":[TD([[subQ4,1.0]])],"derivedFrom":subQ3}),1.0]])]});}
            var Q38;
            {var subQ1=sQuery(id+"F0.wireOp",EDGE,"E41");var subQ3=sQuery(id+"F0.wireOp",EDGE,"E77");var subQ4=makeQuery(id+"F0.imprint","INTERSECT",VERTEX,{"disambiguationData":[OD(0.0)],"derivedFrom":[subQ1,subQ3]});Q38=makeQuery(id+"F0.imprint","IMPRINT",FACE,{"disambiguationData":[TD([[makeQuery(id+"F0.imprint","IMPRINT",EDGE,{"disambiguationData":[TD([[subQ4,-1.0]])],"derivedFrom":subQ3}),1.0]])]});}
            var Q39;
            {var subQ1=sQuery(id+"F0.wireOp",EDGE,"E41");var subQ3=sQuery(id+"F0.wireOp",EDGE,"E77");var subQ4=makeQuery(id+"F0.imprint","INTERSECT",VERTEX,{"disambiguationData":[OD(1.0)],"derivedFrom":[subQ1,subQ3]});Q39=makeQuery(id+"F0.imprint","IMPRINT",FACE,{"disambiguationData":[TD([[makeQuery(id+"F0.imprint","IMPRINT",EDGE,{"disambiguationData":[TD([[subQ4,1.0]])],"derivedFrom":subQ3}),1.0]])]});}
            var Q40;
            {var subQ1=sQuery(id+"F0.wireOp",EDGE,"E41");var subQ3=sQuery(id+"F0.wireOp",EDGE,"E77");var subQ4=makeQuery(id+"F0.imprint","INTERSECT",VERTEX,{"disambiguationData":[OD(1.0)],"derivedFrom":[subQ1,subQ3]});Q40=makeQuery(id+"F0.imprint","IMPRINT",FACE,{"disambiguationData":[TD([[makeQuery(id+"F0.imprint","IMPRINT",EDGE,{"disambiguationData":[TD([[subQ4,-1.0]])],"derivedFrom":subQ3}),1.0]])]});}
            var Q41;
            {var subQ1=sQuery(id+"F0.wireOp",EDGE,"E41");var subQ3=sQuery(id+"F0.wireOp",EDGE,"E82");var subQ4=makeQuery(id+"F0.imprint","INTERSECT",VERTEX,{"disambiguationData":[OD(0.0)],"derivedFrom":[subQ1,subQ3]});Q41=makeQuery(id+"F0.imprint","IMPRINT",FACE,{"disambiguationData":[TD([[makeQuery(id+"F0.imprint","IMPRINT",EDGE,{"disambiguationData":[TD([[subQ4,-1.0]])],"derivedFrom":subQ3}),1.0]])]});}
            var Q42;
            {var subQ1=sQuery(id+"F0.wireOp",EDGE,"E41");var subQ3=sQuery(id+"F0.wireOp",EDGE,"E82");var subQ4=makeQuery(id+"F0.imprint","INTERSECT",VERTEX,{"disambiguationData":[OD(1.0)],"derivedFrom":[subQ1,subQ3]});Q42=makeQuery(id+"F0.imprint","IMPRINT",FACE,{"disambiguationData":[TD([[makeQuery(id+"F0.imprint","IMPRINT",EDGE,{"disambiguationData":[TD([[subQ4,1.0]])],"derivedFrom":subQ3}),1.0]])]});}
            var Q43;
            {var subQ1=sQuery(id+"F0.wireOp",EDGE,"E41");var subQ3=sQuery(id+"F0.wireOp",EDGE,"E82");var subQ4=makeQuery(id+"F0.imprint","INTERSECT",VERTEX,{"disambiguationData":[OD(1.0)],"derivedFrom":[subQ1,subQ3]});Q43=makeQuery(id+"F0.imprint","IMPRINT",FACE,{"disambiguationData":[TD([[makeQuery(id+"F0.imprint","IMPRINT",EDGE,{"disambiguationData":[TD([[subQ4,-1.0]])],"derivedFrom":subQ3}),1.0]])]});}
            var Q44;
            {var subQ1=sQuery(id+"F0.wireOp",EDGE,"E41");var subQ3=sQuery(id+"F0.wireOp",EDGE,"E82");var subQ4=makeQuery(id+"F0.imprint","INTERSECT",VERTEX,{"disambiguationData":[OD(0.0)],"derivedFrom":[subQ1,subQ3]});Q44=makeQuery(id+"F0.imprint","IMPRINT",FACE,{"disambiguationData":[TD([[makeQuery(id+"F0.imprint","IMPRINT",EDGE,{"disambiguationData":[TD([[subQ4,1.0]])],"derivedFrom":subQ3}),1.0]])]});}
            var Q45;
            {var subQ1=sQuery(id+"F0.wireOp",EDGE,"E42");var subQ3=sQuery(id+"F0.wireOp",EDGE,"E78");var subQ4=makeQuery(id+"F0.imprint","INTERSECT",VERTEX,{"disambiguationData":[OD(0.0)],"derivedFrom":[subQ1,subQ3]});Q45=makeQuery(id+"F0.imprint","IMPRINT",FACE,{"disambiguationData":[TD([[makeQuery(id+"F0.imprint","IMPRINT",EDGE,{"disambiguationData":[TD([[subQ4,1.0]])],"derivedFrom":subQ3}),1.0]])]});}
            var Q46;
            {var subQ1=sQuery(id+"F0.wireOp",EDGE,"E42");var subQ3=sQuery(id+"F0.wireOp",EDGE,"E78");var subQ4=makeQuery(id+"F0.imprint","INTERSECT",VERTEX,{"disambiguationData":[OD(0.0)],"derivedFrom":[subQ1,subQ3]});Q46=makeQuery(id+"F0.imprint","IMPRINT",FACE,{"disambiguationData":[TD([[makeQuery(id+"F0.imprint","IMPRINT",EDGE,{"disambiguationData":[TD([[subQ4,-1.0]])],"derivedFrom":subQ3}),1.0]])]});}
            var Q47;
            {var subQ1=sQuery(id+"F0.wireOp",EDGE,"E42");var subQ3=sQuery(id+"F0.wireOp",EDGE,"E78");var subQ4=makeQuery(id+"F0.imprint","INTERSECT",VERTEX,{"disambiguationData":[OD(1.0)],"derivedFrom":[subQ1,subQ3]});Q47=makeQuery(id+"F0.imprint","IMPRINT",FACE,{"disambiguationData":[TD([[makeQuery(id+"F0.imprint","IMPRINT",EDGE,{"disambiguationData":[TD([[subQ4,1.0]])],"derivedFrom":subQ3}),1.0]])]});}
            var Q48;
            {var subQ1=sQuery(id+"F0.wireOp",EDGE,"E42");var subQ3=sQuery(id+"F0.wireOp",EDGE,"E78");var subQ4=makeQuery(id+"F0.imprint","INTERSECT",VERTEX,{"disambiguationData":[OD(1.0)],"derivedFrom":[subQ1,subQ3]});Q48=makeQuery(id+"F0.imprint","IMPRINT",FACE,{"disambiguationData":[TD([[makeQuery(id+"F0.imprint","IMPRINT",EDGE,{"disambiguationData":[TD([[subQ4,-1.0]])],"derivedFrom":subQ3}),1.0]])]});}
            var Q49;
            {var subQ1=sQuery(id+"F0.wireOp",EDGE,"E42");var subQ3=sQuery(id+"F0.wireOp",EDGE,"E54");var subQ4=makeQuery(id+"F0.imprint","INTERSECT",VERTEX,{"disambiguationData":[OD(0.0)],"derivedFrom":[subQ1,subQ3]});Q49=makeQuery(id+"F0.imprint","IMPRINT",FACE,{"disambiguationData":[TD([[makeQuery(id+"F0.imprint","IMPRINT",EDGE,{"disambiguationData":[TD([[subQ4,1.0]])],"derivedFrom":subQ3}),1.0]])]});}
            var Q50;
            {var subQ1=sQuery(id+"F0.wireOp",EDGE,"E42");var subQ3=sQuery(id+"F0.wireOp",EDGE,"E54");var subQ4=makeQuery(id+"F0.imprint","INTERSECT",VERTEX,{"disambiguationData":[OD(0.0)],"derivedFrom":[subQ1,subQ3]});Q50=makeQuery(id+"F0.imprint","IMPRINT",FACE,{"disambiguationData":[TD([[makeQuery(id+"F0.imprint","IMPRINT",EDGE,{"disambiguationData":[TD([[subQ4,-1.0]])],"derivedFrom":subQ3}),1.0]])]});}
            var Q51;
            {var subQ1=sQuery(id+"F0.wireOp",EDGE,"E42");var subQ3=sQuery(id+"F0.wireOp",EDGE,"E54");var subQ4=makeQuery(id+"F0.imprint","INTERSECT",VERTEX,{"disambiguationData":[OD(1.0)],"derivedFrom":[subQ1,subQ3]});Q51=makeQuery(id+"F0.imprint","IMPRINT",FACE,{"disambiguationData":[TD([[makeQuery(id+"F0.imprint","IMPRINT",EDGE,{"disambiguationData":[TD([[subQ4,1.0]])],"derivedFrom":subQ3}),1.0]])]});}
            var Q52;
            {var subQ1=sQuery(id+"F0.wireOp",EDGE,"E42");var subQ3=sQuery(id+"F0.wireOp",EDGE,"E54");var subQ4=makeQuery(id+"F0.imprint","INTERSECT",VERTEX,{"disambiguationData":[OD(1.0)],"derivedFrom":[subQ1,subQ3]});Q52=makeQuery(id+"F0.imprint","IMPRINT",FACE,{"disambiguationData":[TD([[makeQuery(id+"F0.imprint","IMPRINT",EDGE,{"disambiguationData":[TD([[subQ4,-1.0]])],"derivedFrom":subQ3}),1.0]])]});}
            var Q53;
            {var subQ1=sQuery(id+"F0.wireOp",EDGE,"E29");var subQ3=sQuery(id+"F0.wireOp",EDGE,"E55");var subQ4=makeQuery(id+"F0.imprint","INTERSECT",VERTEX,{"derivedFrom":[subQ1,subQ3]});Q53=makeQuery(id+"F0.imprint","IMPRINT",FACE,{"disambiguationData":[TD([[makeQuery(id+"F0.imprint","IMPRINT",EDGE,{"disambiguationData":[TD([[subQ4,-1.0]])],"derivedFrom":subQ3}),1.0]])]});}
            var Q54;
            {var subQ1=sQuery(id+"F0.wireOp",EDGE,"E50");var subQ3=sQuery(id+"F0.wireOp",EDGE,"E55");var subQ4=makeQuery(id+"F0.imprint","INTERSECT",VERTEX,{"derivedFrom":[subQ1,subQ3]});Q54=makeQuery(id+"F0.imprint","IMPRINT",FACE,{"disambiguationData":[TD([[makeQuery(id+"F0.imprint","IMPRINT",EDGE,{"disambiguationData":[TD([[subQ4,-1.0]])],"derivedFrom":subQ3}),1.0]])]});}
            var Q55;
            {var subQ1=sQuery(id+"F0.wireOp",EDGE,"E29");var subQ3=sQuery(id+"F0.wireOp",EDGE,"E55");var subQ4=makeQuery(id+"F0.imprint","INTERSECT",VERTEX,{"derivedFrom":[subQ1,subQ3]});Q55=makeQuery(id+"F0.imprint","IMPRINT",FACE,{"disambiguationData":[TD([[makeQuery(id+"F0.imprint","IMPRINT",EDGE,{"disambiguationData":[TD([[subQ4,1.0]])],"derivedFrom":subQ3}),1.0]])]});}
            var Q56;
            {var subQ1=sQuery(id+"F0.wireOp",EDGE,"E59");var subQ3=sQuery(id+"F0.wireOp",EDGE,"E79");var subQ4=makeQuery(id+"F0.imprint","INTERSECT",VERTEX,{"derivedFrom":[subQ1,subQ3]});Q56=makeQuery(id+"F0.imprint","IMPRINT",FACE,{"disambiguationData":[TD([[makeQuery(id+"F0.imprint","IMPRINT",EDGE,{"disambiguationData":[TD([[subQ4,1.0]])],"derivedFrom":subQ3}),1.0]])]});}
            var Q57;
            {var subQ1=sQuery(id+"F0.wireOp",EDGE,"E60");var subQ3=sQuery(id+"F0.wireOp",EDGE,"E79");var subQ4=makeQuery(id+"F0.imprint","INTERSECT",VERTEX,{"derivedFrom":[subQ1,subQ3]});Q57=makeQuery(id+"F0.imprint","IMPRINT",FACE,{"disambiguationData":[TD([[makeQuery(id+"F0.imprint","IMPRINT",EDGE,{"disambiguationData":[TD([[subQ4,1.0]])],"derivedFrom":subQ3}),1.0]])]});}
            var Q58;
            {var subQ1=sQuery(id+"F0.wireOp",EDGE,"E59");var subQ3=sQuery(id+"F0.wireOp",EDGE,"E79");var subQ4=makeQuery(id+"F0.imprint","INTERSECT",VERTEX,{"derivedFrom":[subQ1,subQ3]});Q58=makeQuery(id+"F0.imprint","IMPRINT",FACE,{"disambiguationData":[TD([[makeQuery(id+"F0.imprint","IMPRINT",EDGE,{"disambiguationData":[TD([[subQ4,-1.0]])],"derivedFrom":subQ3}),1.0]])]});}
            var Q59;
            {var subQ1=sQuery(id+"F0.wireOp",EDGE,"E28");var subQ3=sQuery(id+"F0.wireOp",EDGE,"E80");var subQ4=makeQuery(id+"F0.imprint","INTERSECT",VERTEX,{"derivedFrom":[subQ1,subQ3]});Q59=makeQuery(id+"F0.imprint","IMPRINT",FACE,{"disambiguationData":[TD([[makeQuery(id+"F0.imprint","IMPRINT",EDGE,{"disambiguationData":[TD([[subQ4,-1.0]])],"derivedFrom":subQ3}),1.0]])]});}
            var Q60;
            {var subQ1=sQuery(id+"F0.wireOp",EDGE,"E60");var subQ3=sQuery(id+"F0.wireOp",EDGE,"E80");var subQ4=makeQuery(id+"F0.imprint","INTERSECT",VERTEX,{"derivedFrom":[subQ1,subQ3]});Q60=makeQuery(id+"F0.imprint","IMPRINT",FACE,{"disambiguationData":[TD([[makeQuery(id+"F0.imprint","IMPRINT",EDGE,{"disambiguationData":[TD([[subQ4,-1.0]])],"derivedFrom":subQ3}),1.0]])]});}
            var Q61;
            {var subQ1=sQuery(id+"F0.wireOp",EDGE,"E28");var subQ3=sQuery(id+"F0.wireOp",EDGE,"E80");var subQ4=makeQuery(id+"F0.imprint","INTERSECT",VERTEX,{"derivedFrom":[subQ1,subQ3]});Q61=makeQuery(id+"F0.imprint","IMPRINT",FACE,{"disambiguationData":[TD([[makeQuery(id+"F0.imprint","IMPRINT",EDGE,{"disambiguationData":[TD([[subQ4,1.0]])],"derivedFrom":subQ3}),1.0]])]});}
            var Q62;
            {var subQ1=sQuery(id+"F0.wireOp",EDGE,"E42");var subQ3=sQuery(id+"F0.wireOp",EDGE,"E81");var subQ4=makeQuery(id+"F0.imprint","INTERSECT",VERTEX,{"disambiguationData":[OD(1.0)],"derivedFrom":[subQ1,subQ3]});Q62=makeQuery(id+"F0.imprint","IMPRINT",FACE,{"disambiguationData":[TD([[makeQuery(id+"F0.imprint","IMPRINT",EDGE,{"disambiguationData":[TD([[subQ4,1.0]])],"derivedFrom":subQ3}),1.0]])]});}
            var Q63;
            {var subQ1=sQuery(id+"F0.wireOp",EDGE,"E42");var subQ3=sQuery(id+"F0.wireOp",EDGE,"E81");var subQ4=makeQuery(id+"F0.imprint","INTERSECT",VERTEX,{"disambiguationData":[OD(1.0)],"derivedFrom":[subQ1,subQ3]});Q63=makeQuery(id+"F0.imprint","IMPRINT",FACE,{"disambiguationData":[TD([[makeQuery(id+"F0.imprint","IMPRINT",EDGE,{"disambiguationData":[TD([[subQ4,-1.0]])],"derivedFrom":subQ3}),1.0]])]});}
            var Q64;
            {var subQ1=sQuery(id+"F0.wireOp",EDGE,"E42");var subQ3=sQuery(id+"F0.wireOp",EDGE,"E81");var subQ4=makeQuery(id+"F0.imprint","INTERSECT",VERTEX,{"disambiguationData":[OD(0.0)],"derivedFrom":[subQ1,subQ3]});Q64=makeQuery(id+"F0.imprint","IMPRINT",FACE,{"disambiguationData":[TD([[makeQuery(id+"F0.imprint","IMPRINT",EDGE,{"disambiguationData":[TD([[subQ4,1.0]])],"derivedFrom":subQ3}),1.0]])]});}
            var Q65;
            {var subQ1=sQuery(id+"F0.wireOp",EDGE,"E42");var subQ3=sQuery(id+"F0.wireOp",EDGE,"E81");var subQ4=makeQuery(id+"F0.imprint","INTERSECT",VERTEX,{"disambiguationData":[OD(0.0)],"derivedFrom":[subQ1,subQ3]});Q65=makeQuery(id+"F0.imprint","IMPRINT",FACE,{"disambiguationData":[TD([[makeQuery(id+"F0.imprint","IMPRINT",EDGE,{"disambiguationData":[TD([[subQ4,-1.0]])],"derivedFrom":subQ3}),1.0]])]});}
            var Q66;
            {var subQ1=sQuery(id+"F0.wireOp",EDGE,"E36");var subQ3=sQuery(id+"F0.wireOp",EDGE,"E45");var subQ4=makeQuery(id+"F0.imprint","INTERSECT",VERTEX,{"derivedFrom":[subQ1,subQ3]});Q66=makeQuery(id+"F0.imprint","IMPRINT",FACE,{"disambiguationData":[TD([[makeQuery(id+"F0.imprint","IMPRINT",EDGE,{"disambiguationData":[TD([[subQ4,-1.0]])],"derivedFrom":subQ3}),1.0]])]});}
            var Q67;
            {var subQ1=sQuery(id+"F0.wireOp",EDGE,"E27");var subQ3=sQuery(id+"F0.wireOp",EDGE,"E45");var subQ4=makeQuery(id+"F0.imprint","INTERSECT",VERTEX,{"derivedFrom":[subQ1,subQ3]});Q67=makeQuery(id+"F0.imprint","IMPRINT",FACE,{"disambiguationData":[TD([[makeQuery(id+"F0.imprint","IMPRINT",EDGE,{"disambiguationData":[TD([[subQ4,1.0]])],"derivedFrom":subQ3}),1.0]])]});}
            var Q68;
            {var subQ1=sQuery(id+"F0.wireOp",EDGE,"E27");var subQ3=sQuery(id+"F0.wireOp",EDGE,"E45");var subQ4=makeQuery(id+"F0.imprint","INTERSECT",VERTEX,{"derivedFrom":[subQ1,subQ3]});Q68=makeQuery(id+"F0.imprint","IMPRINT",FACE,{"disambiguationData":[TD([[makeQuery(id+"F0.imprint","IMPRINT",EDGE,{"disambiguationData":[TD([[subQ4,-1.0]])],"derivedFrom":subQ3}),1.0]])]});}
            var Q69;
            {var subQ1=sQuery(id+"F0.wireOp",EDGE,"E27");var subQ3=sQuery(id+"F0.wireOp",EDGE,"E44");var subQ4=makeQuery(id+"F0.imprint","INTERSECT",VERTEX,{"derivedFrom":[subQ1,subQ3]});Q69=makeQuery(id+"F0.imprint","IMPRINT",FACE,{"disambiguationData":[TD([[makeQuery(id+"F0.imprint","IMPRINT",EDGE,{"disambiguationData":[TD([[subQ4,1.0]])],"derivedFrom":subQ3}),1.0]])]});}
            var Q70;
            {var subQ1=sQuery(id+"F0.wireOp",EDGE,"E27");var subQ3=sQuery(id+"F0.wireOp",EDGE,"E44");var subQ4=makeQuery(id+"F0.imprint","INTERSECT",VERTEX,{"derivedFrom":[subQ1,subQ3]});Q70=makeQuery(id+"F0.imprint","IMPRINT",FACE,{"disambiguationData":[TD([[makeQuery(id+"F0.imprint","IMPRINT",EDGE,{"disambiguationData":[TD([[subQ4,-1.0]])],"derivedFrom":subQ3}),1.0]])]});}
            var Q71;
            {var subQ1=sQuery(id+"F0.wireOp",EDGE,"E38");var subQ3=sQuery(id+"F0.wireOp",EDGE,"E44");var subQ4=makeQuery(id+"F0.imprint","INTERSECT",VERTEX,{"derivedFrom":[subQ1,subQ3]});Q71=makeQuery(id+"F0.imprint","IMPRINT",FACE,{"disambiguationData":[TD([[makeQuery(id+"F0.imprint","IMPRINT",EDGE,{"disambiguationData":[TD([[subQ4,1.0]])],"derivedFrom":subQ3}),1.0]])]});}
            extrude(context, id + "F13", {"entities" : qUnion([Q0, Q1, Q2, Q3, Q4, Q5, Q6, Q7, Q8, Q9, Q10, Q11, Q12, Q13, Q14, Q15, Q16, Q17, Q18, Q19, Q20, Q21, Q22, Q23, Q24, Q25, Q26, Q27, Q28, Q29, Q30, Q31, Q32, Q33, Q34, Q35, Q36, Q37, Q38, Q39, Q40, Q41, Q42, Q43, Q44, Q45, Q46, Q47, Q48, Q49, Q50, Q51, Q52, Q53, Q54, Q55, Q56, Q57, Q58, Q59, Q60, Q61, Q62, Q63, Q64, Q65, Q66, Q67, Q68, Q69, Q70, Q71]), "operationType" : NewBodyOperationType.REMOVE, "endBound" : BoundingType.THROUGH_ALL, "oppositeDirection" : true, "depth" : 25 * mm, "offsetDistance" : 25 * mm});
        }
        {
            var Q0;
            Q0=makeQuery(id+"F0.imprint","IMPRINT",FACE,{"disambiguationData":[TD([[makeQuery(id+"F0.imprint","IMPRINT",EDGE,{"derivedFrom":sQuery(id+"F0.wireOp",EDGE,"E15")}),1.0]])]});
            var Q1;
            {var subQ2=sQuery(id+"F0.wireOp",EDGE,"E11");Q1=makeQuery(id+"F0.imprint","IMPRINT",FACE,{"disambiguationData":[TD([[makeQuery(id+"F0.imprint","IMPRINT",EDGE,{"derivedFrom":subQ2}),1.0]])]});}
            extrude(context, id + "F14", {"entities" : qUnion([Q0, Q1]), "operationType" : NewBodyOperationType.ADD, "depth" : 35 * mm, "offsetDistance" : 25 * mm});
        }
        {
            var Q0;
            {var subQ1=sQuery(id+"F0.wireOp",EDGE,"E35");var subQ3=sQuery(id+"F0.wireOp",EDGE,"E92");var subQ4=makeQuery(id+"F0.imprint","INTERSECT",VERTEX,{"derivedFrom":[subQ1,subQ3]});Q0=makeQuery(id+"F0.imprint","IMPRINT",FACE,{"disambiguationData":[TD([[makeQuery(id+"F0.imprint","IMPRINT",EDGE,{"disambiguationData":[TD([[subQ4,1.0]])],"derivedFrom":subQ3}),1.0]])]});}
            var Q1;
            {var subQ1=sQuery(id+"F0.wireOp",EDGE,"E36");var subQ3=sQuery(id+"F0.wireOp",EDGE,"E92");var subQ4=makeQuery(id+"F0.imprint","INTERSECT",VERTEX,{"derivedFrom":[subQ1,subQ3]});Q1=makeQuery(id+"F0.imprint","IMPRINT",FACE,{"disambiguationData":[TD([[makeQuery(id+"F0.imprint","IMPRINT",EDGE,{"disambiguationData":[TD([[subQ4,1.0]])],"derivedFrom":subQ3}),1.0]])]});}
            var Q2;
            {var subQ1=sQuery(id+"F0.wireOp",EDGE,"E35");var subQ3=sQuery(id+"F0.wireOp",EDGE,"E92");var subQ4=makeQuery(id+"F0.imprint","INTERSECT",VERTEX,{"derivedFrom":[subQ1,subQ3]});Q2=makeQuery(id+"F0.imprint","IMPRINT",FACE,{"disambiguationData":[TD([[makeQuery(id+"F0.imprint","IMPRINT",EDGE,{"disambiguationData":[TD([[subQ4,-1.0]])],"derivedFrom":subQ3}),1.0]])]});}
            var Q3;
            {var subQ1=sQuery(id+"F0.wireOp",EDGE,"E37");var subQ3=sQuery(id+"F0.wireOp",EDGE,"E91");var subQ4=makeQuery(id+"F0.imprint","INTERSECT",VERTEX,{"derivedFrom":[subQ1,subQ3]});Q3=makeQuery(id+"F0.imprint","IMPRINT",FACE,{"disambiguationData":[TD([[makeQuery(id+"F0.imprint","IMPRINT",EDGE,{"disambiguationData":[TD([[subQ4,-1.0]])],"derivedFrom":subQ3}),1.0]])]});}
            var Q4;
            {var subQ1=sQuery(id+"F0.wireOp",EDGE,"E38");var subQ3=sQuery(id+"F0.wireOp",EDGE,"E91");var subQ4=makeQuery(id+"F0.imprint","INTERSECT",VERTEX,{"derivedFrom":[subQ1,subQ3]});Q4=makeQuery(id+"F0.imprint","IMPRINT",FACE,{"disambiguationData":[TD([[makeQuery(id+"F0.imprint","IMPRINT",EDGE,{"disambiguationData":[TD([[subQ4,-1.0]])],"derivedFrom":subQ3}),1.0]])]});}
            var Q5;
            {var subQ1=sQuery(id+"F0.wireOp",EDGE,"E37");var subQ3=sQuery(id+"F0.wireOp",EDGE,"E91");var subQ4=makeQuery(id+"F0.imprint","INTERSECT",VERTEX,{"derivedFrom":[subQ1,subQ3]});Q5=makeQuery(id+"F0.imprint","IMPRINT",FACE,{"disambiguationData":[TD([[makeQuery(id+"F0.imprint","IMPRINT",EDGE,{"disambiguationData":[TD([[subQ4,1.0]])],"derivedFrom":subQ3}),1.0]])]});}
            var Q6;
            {var subQ1=sQuery(id+"F0.wireOp",EDGE,"E83");var subQ3=sQuery(id+"F0.wireOp",EDGE,"E88");var subQ4=makeQuery(id+"F0.imprint","INTERSECT",VERTEX,{"derivedFrom":[subQ1,subQ3]});Q6=makeQuery(id+"F0.imprint","IMPRINT",FACE,{"disambiguationData":[TD([[makeQuery(id+"F0.imprint","IMPRINT",EDGE,{"disambiguationData":[TD([[subQ4,1.0]])],"derivedFrom":subQ3}),1.0]])]});}
            var Q7;
            {var subQ1=sQuery(id+"F0.wireOp",EDGE,"E27");var subQ3=sQuery(id+"F0.wireOp",EDGE,"E88");var subQ4=makeQuery(id+"F0.imprint","INTERSECT",VERTEX,{"derivedFrom":[subQ1,subQ3]});Q7=makeQuery(id+"F0.imprint","IMPRINT",FACE,{"disambiguationData":[TD([[makeQuery(id+"F0.imprint","IMPRINT",EDGE,{"disambiguationData":[TD([[subQ4,-1.0]])],"derivedFrom":subQ3}),1.0]])]});}
            var Q8;
            {var subQ1=sQuery(id+"F0.wireOp",EDGE,"E27");var subQ3=sQuery(id+"F0.wireOp",EDGE,"E88");var subQ4=makeQuery(id+"F0.imprint","INTERSECT",VERTEX,{"derivedFrom":[subQ1,subQ3]});Q8=makeQuery(id+"F0.imprint","IMPRINT",FACE,{"disambiguationData":[TD([[makeQuery(id+"F0.imprint","IMPRINT",EDGE,{"disambiguationData":[TD([[subQ4,1.0]])],"derivedFrom":subQ3}),1.0]])]});}
            var Q9;
            {var subQ1=sQuery(id+"F0.wireOp",EDGE,"E62");var subQ3=sQuery(id+"F0.wireOp",EDGE,"E89");var subQ4=makeQuery(id+"F0.imprint","INTERSECT",VERTEX,{"disambiguationData":[OD(1.0)],"derivedFrom":[subQ1,subQ3]});Q9=makeQuery(id+"F0.imprint","IMPRINT",FACE,{"disambiguationData":[TD([[makeQuery(id+"F0.imprint","IMPRINT",EDGE,{"disambiguationData":[TD([[subQ4,-1.0]])],"derivedFrom":subQ3}),1.0]])]});}
            var Q10;
            {var subQ1=sQuery(id+"F0.wireOp",EDGE,"E62");var subQ3=sQuery(id+"F0.wireOp",EDGE,"E89");var subQ4=makeQuery(id+"F0.imprint","INTERSECT",VERTEX,{"disambiguationData":[OD(1.0)],"derivedFrom":[subQ1,subQ3]});Q10=makeQuery(id+"F0.imprint","IMPRINT",FACE,{"disambiguationData":[TD([[makeQuery(id+"F0.imprint","IMPRINT",EDGE,{"disambiguationData":[TD([[subQ4,1.0]])],"derivedFrom":subQ3}),1.0]])]});}
            var Q11;
            {var subQ1=sQuery(id+"F0.wireOp",EDGE,"E62");var subQ3=sQuery(id+"F0.wireOp",EDGE,"E89");var subQ4=makeQuery(id+"F0.imprint","INTERSECT",VERTEX,{"disambiguationData":[OD(0.0)],"derivedFrom":[subQ1,subQ3]});Q11=makeQuery(id+"F0.imprint","IMPRINT",FACE,{"disambiguationData":[TD([[makeQuery(id+"F0.imprint","IMPRINT",EDGE,{"disambiguationData":[TD([[subQ4,-1.0]])],"derivedFrom":subQ3}),1.0]])]});}
            var Q12;
            {var subQ1=sQuery(id+"F0.wireOp",EDGE,"E62");var subQ3=sQuery(id+"F0.wireOp",EDGE,"E89");var subQ4=makeQuery(id+"F0.imprint","INTERSECT",VERTEX,{"disambiguationData":[OD(0.0)],"derivedFrom":[subQ1,subQ3]});Q12=makeQuery(id+"F0.imprint","IMPRINT",FACE,{"disambiguationData":[TD([[makeQuery(id+"F0.imprint","IMPRINT",EDGE,{"disambiguationData":[TD([[subQ4,1.0]])],"derivedFrom":subQ3}),1.0]])]});}
            var Q13;
            {var subQ1=sQuery(id+"F0.wireOp",EDGE,"E48");var subQ3=sQuery(id+"F0.wireOp",EDGE,"E90");var subQ4=makeQuery(id+"F0.imprint","INTERSECT",VERTEX,{"disambiguationData":[OD(1.0)],"derivedFrom":[subQ1,subQ3]});Q13=makeQuery(id+"F0.imprint","IMPRINT",FACE,{"disambiguationData":[TD([[makeQuery(id+"F0.imprint","IMPRINT",EDGE,{"disambiguationData":[TD([[subQ4,1.0]])],"derivedFrom":subQ3}),1.0]])]});}
            var Q14;
            {var subQ1=sQuery(id+"F0.wireOp",EDGE,"E48");var subQ3=sQuery(id+"F0.wireOp",EDGE,"E90");var subQ4=makeQuery(id+"F0.imprint","INTERSECT",VERTEX,{"disambiguationData":[OD(0.0)],"derivedFrom":[subQ1,subQ3]});Q14=makeQuery(id+"F0.imprint","IMPRINT",FACE,{"disambiguationData":[TD([[makeQuery(id+"F0.imprint","IMPRINT",EDGE,{"disambiguationData":[TD([[subQ4,-1.0]])],"derivedFrom":subQ3}),1.0]])]});}
            var Q15;
            {var subQ1=sQuery(id+"F0.wireOp",EDGE,"E48");var subQ3=sQuery(id+"F0.wireOp",EDGE,"E90");var subQ4=makeQuery(id+"F0.imprint","INTERSECT",VERTEX,{"disambiguationData":[OD(0.0)],"derivedFrom":[subQ1,subQ3]});Q15=makeQuery(id+"F0.imprint","IMPRINT",FACE,{"disambiguationData":[TD([[makeQuery(id+"F0.imprint","IMPRINT",EDGE,{"disambiguationData":[TD([[subQ4,1.0]])],"derivedFrom":subQ3}),1.0]])]});}
            var Q16;
            {var subQ1=sQuery(id+"F0.wireOp",EDGE,"E48");var subQ3=sQuery(id+"F0.wireOp",EDGE,"E90");var subQ4=makeQuery(id+"F0.imprint","INTERSECT",VERTEX,{"disambiguationData":[OD(1.0)],"derivedFrom":[subQ1,subQ3]});Q16=makeQuery(id+"F0.imprint","IMPRINT",FACE,{"disambiguationData":[TD([[makeQuery(id+"F0.imprint","IMPRINT",EDGE,{"disambiguationData":[TD([[subQ4,-1.0]])],"derivedFrom":subQ3}),1.0]])]});}
            extrude(context, id + "F15", {"entities" : qUnion([Q0, Q1, Q2, Q3, Q4, Q5, Q6, Q7, Q8, Q9, Q10, Q11, Q12, Q13, Q14, Q15, Q16]), "operationType" : NewBodyOperationType.REMOVE, "oppositeDirection" : true, "depth" : 25 * mm, "offsetDistance" : 25 * mm});
        }
        {
            var Q0;
            {var subQ1=sQuery(id+"F0.wireOp",EDGE,"E27");var subQ3=sQuery(id+"F0.wireOp",EDGE,"E88");var subQ4=makeQuery(id+"F0.imprint","INTERSECT",VERTEX,{"derivedFrom":[subQ1,subQ3]});Q0=makeQuery(id+"F0.imprint","IMPRINT",FACE,{"disambiguationData":[TD([[makeQuery(id+"F0.imprint","IMPRINT",EDGE,{"disambiguationData":[TD([[subQ4,1.0]])],"derivedFrom":subQ3}),1.0]])]});}
            var Q1;
            {var subQ1=sQuery(id+"F0.wireOp",EDGE,"E27");var subQ3=sQuery(id+"F0.wireOp",EDGE,"E88");var subQ4=makeQuery(id+"F0.imprint","INTERSECT",VERTEX,{"derivedFrom":[subQ1,subQ3]});Q1=makeQuery(id+"F0.imprint","IMPRINT",FACE,{"disambiguationData":[TD([[makeQuery(id+"F0.imprint","IMPRINT",EDGE,{"disambiguationData":[TD([[subQ4,-1.0]])],"derivedFrom":subQ3}),1.0]])]});}
            var Q2;
            {var subQ1=sQuery(id+"F0.wireOp",EDGE,"E83");var subQ3=sQuery(id+"F0.wireOp",EDGE,"E88");var subQ4=makeQuery(id+"F0.imprint","INTERSECT",VERTEX,{"derivedFrom":[subQ1,subQ3]});Q2=makeQuery(id+"F0.imprint","IMPRINT",FACE,{"disambiguationData":[TD([[makeQuery(id+"F0.imprint","IMPRINT",EDGE,{"disambiguationData":[TD([[subQ4,1.0]])],"derivedFrom":subQ3}),1.0]])]});}
            var Q3;
            {var subQ1=sQuery(id+"F0.wireOp",EDGE,"E37");var subQ3=sQuery(id+"F0.wireOp",EDGE,"E91");var subQ4=makeQuery(id+"F0.imprint","INTERSECT",VERTEX,{"derivedFrom":[subQ1,subQ3]});Q3=makeQuery(id+"F0.imprint","IMPRINT",FACE,{"disambiguationData":[TD([[makeQuery(id+"F0.imprint","IMPRINT",EDGE,{"disambiguationData":[TD([[subQ4,-1.0]])],"derivedFrom":subQ3}),1.0]])]});}
            var Q4;
            {var subQ1=sQuery(id+"F0.wireOp",EDGE,"E38");var subQ3=sQuery(id+"F0.wireOp",EDGE,"E91");var subQ4=makeQuery(id+"F0.imprint","INTERSECT",VERTEX,{"derivedFrom":[subQ1,subQ3]});Q4=makeQuery(id+"F0.imprint","IMPRINT",FACE,{"disambiguationData":[TD([[makeQuery(id+"F0.imprint","IMPRINT",EDGE,{"disambiguationData":[TD([[subQ4,-1.0]])],"derivedFrom":subQ3}),1.0]])]});}
            var Q5;
            {var subQ1=sQuery(id+"F0.wireOp",EDGE,"E37");var subQ3=sQuery(id+"F0.wireOp",EDGE,"E91");var subQ4=makeQuery(id+"F0.imprint","INTERSECT",VERTEX,{"derivedFrom":[subQ1,subQ3]});Q5=makeQuery(id+"F0.imprint","IMPRINT",FACE,{"disambiguationData":[TD([[makeQuery(id+"F0.imprint","IMPRINT",EDGE,{"disambiguationData":[TD([[subQ4,1.0]])],"derivedFrom":subQ3}),1.0]])]});}
            var Q6;
            {var subQ1=sQuery(id+"F0.wireOp",EDGE,"E35");var subQ3=sQuery(id+"F0.wireOp",EDGE,"E92");var subQ4=makeQuery(id+"F0.imprint","INTERSECT",VERTEX,{"derivedFrom":[subQ1,subQ3]});Q6=makeQuery(id+"F0.imprint","IMPRINT",FACE,{"disambiguationData":[TD([[makeQuery(id+"F0.imprint","IMPRINT",EDGE,{"disambiguationData":[TD([[subQ4,-1.0]])],"derivedFrom":subQ3}),1.0]])]});}
            var Q7;
            {var subQ1=sQuery(id+"F0.wireOp",EDGE,"E36");var subQ3=sQuery(id+"F0.wireOp",EDGE,"E92");var subQ4=makeQuery(id+"F0.imprint","INTERSECT",VERTEX,{"derivedFrom":[subQ1,subQ3]});Q7=makeQuery(id+"F0.imprint","IMPRINT",FACE,{"disambiguationData":[TD([[makeQuery(id+"F0.imprint","IMPRINT",EDGE,{"disambiguationData":[TD([[subQ4,1.0]])],"derivedFrom":subQ3}),1.0]])]});}
            var Q8;
            {var subQ1=sQuery(id+"F0.wireOp",EDGE,"E35");var subQ3=sQuery(id+"F0.wireOp",EDGE,"E92");var subQ4=makeQuery(id+"F0.imprint","INTERSECT",VERTEX,{"derivedFrom":[subQ1,subQ3]});Q8=makeQuery(id+"F0.imprint","IMPRINT",FACE,{"disambiguationData":[TD([[makeQuery(id+"F0.imprint","IMPRINT",EDGE,{"disambiguationData":[TD([[subQ4,1.0]])],"derivedFrom":subQ3}),1.0]])]});}
            var Q9;
            {var subQ1=sQuery(id+"F0.wireOp",EDGE,"E62");var subQ3=sQuery(id+"F0.wireOp",EDGE,"E89");var subQ4=makeQuery(id+"F0.imprint","INTERSECT",VERTEX,{"disambiguationData":[OD(0.0)],"derivedFrom":[subQ1,subQ3]});Q9=makeQuery(id+"F0.imprint","IMPRINT",FACE,{"disambiguationData":[TD([[makeQuery(id+"F0.imprint","IMPRINT",EDGE,{"disambiguationData":[TD([[subQ4,1.0]])],"derivedFrom":subQ3}),1.0]])]});}
            var Q10;
            {var subQ1=sQuery(id+"F0.wireOp",EDGE,"E62");var subQ3=sQuery(id+"F0.wireOp",EDGE,"E89");var subQ4=makeQuery(id+"F0.imprint","INTERSECT",VERTEX,{"disambiguationData":[OD(0.0)],"derivedFrom":[subQ1,subQ3]});Q10=makeQuery(id+"F0.imprint","IMPRINT",FACE,{"disambiguationData":[TD([[makeQuery(id+"F0.imprint","IMPRINT",EDGE,{"disambiguationData":[TD([[subQ4,-1.0]])],"derivedFrom":subQ3}),1.0]])]});}
            var Q11;
            {var subQ1=sQuery(id+"F0.wireOp",EDGE,"E62");var subQ3=sQuery(id+"F0.wireOp",EDGE,"E89");var subQ4=makeQuery(id+"F0.imprint","INTERSECT",VERTEX,{"disambiguationData":[OD(1.0)],"derivedFrom":[subQ1,subQ3]});Q11=makeQuery(id+"F0.imprint","IMPRINT",FACE,{"disambiguationData":[TD([[makeQuery(id+"F0.imprint","IMPRINT",EDGE,{"disambiguationData":[TD([[subQ4,1.0]])],"derivedFrom":subQ3}),1.0]])]});}
            var Q12;
            {var subQ1=sQuery(id+"F0.wireOp",EDGE,"E62");var subQ3=sQuery(id+"F0.wireOp",EDGE,"E89");var subQ4=makeQuery(id+"F0.imprint","INTERSECT",VERTEX,{"disambiguationData":[OD(1.0)],"derivedFrom":[subQ1,subQ3]});Q12=makeQuery(id+"F0.imprint","IMPRINT",FACE,{"disambiguationData":[TD([[makeQuery(id+"F0.imprint","IMPRINT",EDGE,{"disambiguationData":[TD([[subQ4,-1.0]])],"derivedFrom":subQ3}),1.0]])]});}
            var Q13;
            {var subQ1=sQuery(id+"F0.wireOp",EDGE,"E48");var subQ3=sQuery(id+"F0.wireOp",EDGE,"E90");var subQ4=makeQuery(id+"F0.imprint","INTERSECT",VERTEX,{"disambiguationData":[OD(1.0)],"derivedFrom":[subQ1,subQ3]});Q13=makeQuery(id+"F0.imprint","IMPRINT",FACE,{"disambiguationData":[TD([[makeQuery(id+"F0.imprint","IMPRINT",EDGE,{"disambiguationData":[TD([[subQ4,1.0]])],"derivedFrom":subQ3}),1.0]])]});}
            var Q14;
            {var subQ1=sQuery(id+"F0.wireOp",EDGE,"E48");var subQ3=sQuery(id+"F0.wireOp",EDGE,"E90");var subQ4=makeQuery(id+"F0.imprint","INTERSECT",VERTEX,{"disambiguationData":[OD(0.0)],"derivedFrom":[subQ1,subQ3]});Q14=makeQuery(id+"F0.imprint","IMPRINT",FACE,{"disambiguationData":[TD([[makeQuery(id+"F0.imprint","IMPRINT",EDGE,{"disambiguationData":[TD([[subQ4,-1.0]])],"derivedFrom":subQ3}),1.0]])]});}
            var Q15;
            {var subQ1=sQuery(id+"F0.wireOp",EDGE,"E48");var subQ3=sQuery(id+"F0.wireOp",EDGE,"E90");var subQ4=makeQuery(id+"F0.imprint","INTERSECT",VERTEX,{"disambiguationData":[OD(0.0)],"derivedFrom":[subQ1,subQ3]});Q15=makeQuery(id+"F0.imprint","IMPRINT",FACE,{"disambiguationData":[TD([[makeQuery(id+"F0.imprint","IMPRINT",EDGE,{"disambiguationData":[TD([[subQ4,1.0]])],"derivedFrom":subQ3}),1.0]])]});}
            var Q16;
            {var subQ1=sQuery(id+"F0.wireOp",EDGE,"E48");var subQ3=sQuery(id+"F0.wireOp",EDGE,"E90");var subQ4=makeQuery(id+"F0.imprint","INTERSECT",VERTEX,{"disambiguationData":[OD(1.0)],"derivedFrom":[subQ1,subQ3]});Q16=makeQuery(id+"F0.imprint","IMPRINT",FACE,{"disambiguationData":[TD([[makeQuery(id+"F0.imprint","IMPRINT",EDGE,{"disambiguationData":[TD([[subQ4,-1.0]])],"derivedFrom":subQ3}),1.0]])]});}
            extrude(context, id + "F16", {"entities" : qUnion([Q0, Q1, Q2, Q3, Q4, Q5, Q6, Q7, Q8, Q9, Q10, Q11, Q12, Q13, Q14, Q15, Q16]), "operationType" : NewBodyOperationType.REMOVE, "depth" : 25 * mm, "offsetDistance" : 25 * mm});
        }
    });
